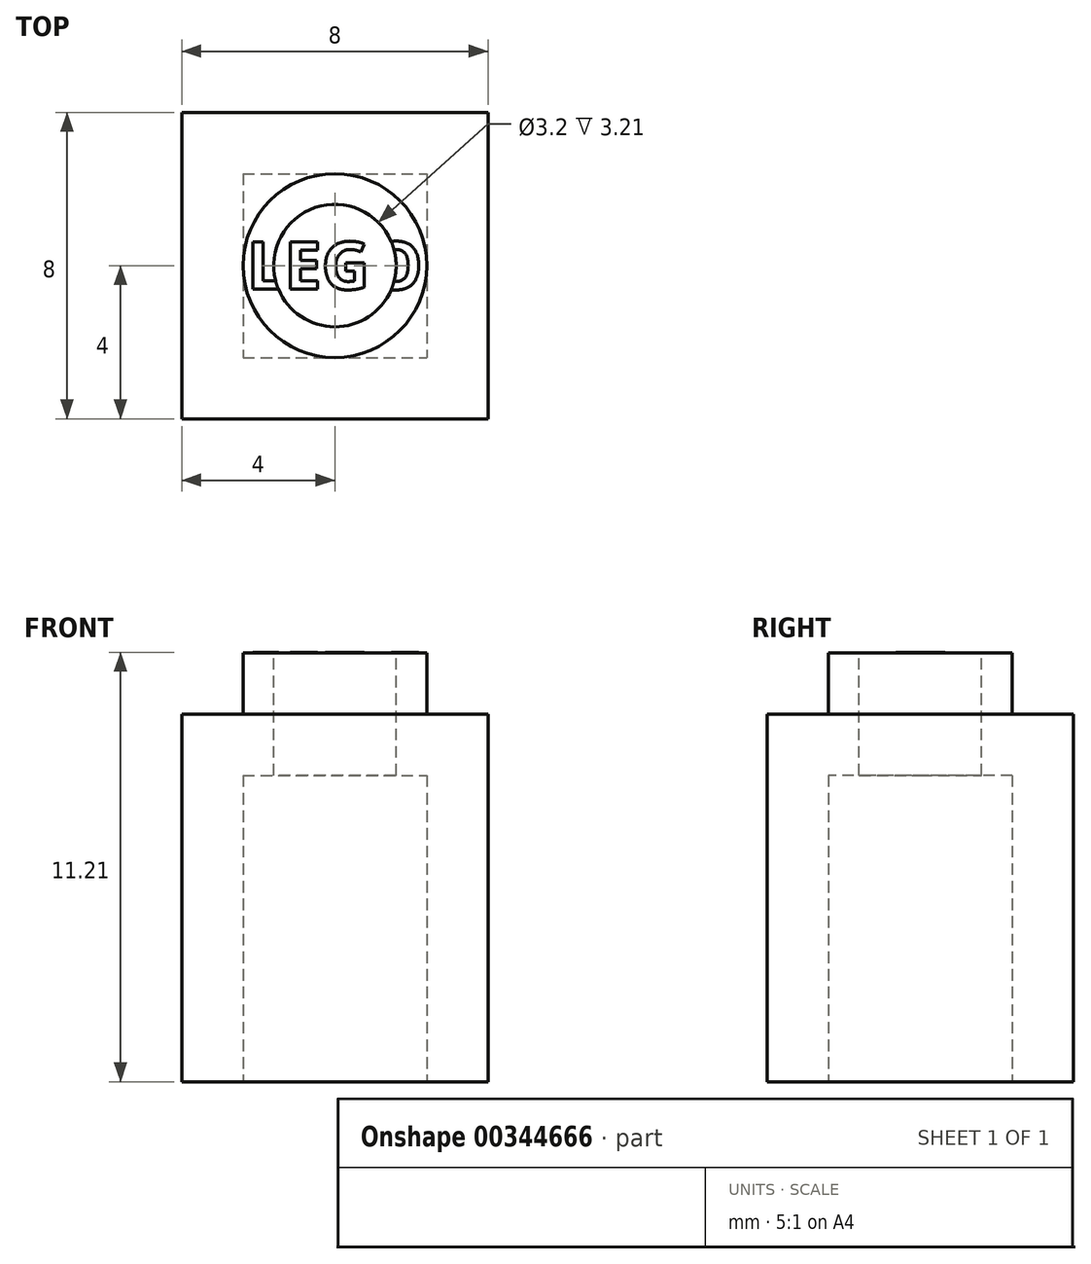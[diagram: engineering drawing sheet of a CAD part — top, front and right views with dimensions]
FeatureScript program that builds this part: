
annotation { "Feature Type Name" : "Feature", "Feature Type Description" : "" }
export const myFeature = defineFeature(function(context is Context, id is Id, definition is map)
    precondition{}
    {
        {
            var Q0;
            Q0=qCreatedBy(makeId("Top.planeOp"),FACE);
            var sketch = newSketch(context, id + "F0", { "sketchPlane" : qUnion([Q0])});
            skLineSegment(sketch, "E0.bottom", {"start": v(-4, 4) * mm, "end": v(4, 4) * mm});
            skLineSegment(sketch, "E0.top", {"start": v(-4, -4) * mm, "end": v(4, -4) * mm});
            skLineSegment(sketch, "E0.left", {"start": v(-4, 4) * mm, "end": v(-4, -4) * mm});
            skLineSegment(sketch, "E0.right", {"start": v(4, 4) * mm, "end": v(4, -4) * mm});
            skPoint(sketch, "E0.middle", {"position": v(0, 0) * mm});
            skSolve(sketch);
        }
        {
            var Q0;
            Q0=makeQuery(id+"F0.imprint","IMPRINT",FACE,{"disambiguationData":[TD([[makeQuery(id+"F0.imprint","IMPRINT",EDGE,{"derivedFrom":sQuery(id+"F0.wireOp",EDGE,"E0.bottom")}),-1.0]])]});
            extrude(context, id + "F1", {"entities" : qUnion([Q0]), "depth" : 9.6 * mm});
        }
        {
            var Q0;
            Q0=makeQuery(id+"F1.opExtrude","CAP_FACE",FACE,{"disambiguationData":[OSD([sQuery(id+"F0.wireOp",EDGE,"E0.bottom"),sQuery(id+"F0.wireOp",EDGE,"E0.top"),sQuery(id+"F0.wireOp",EDGE,"E0.left"),sQuery(id+"F0.wireOp",EDGE,"E0.right")])],"isStart":true});
            var sketch = newSketch(context, id + "F2", { "sketchPlane" : qUnion([Q0])});
            skLineSegment(sketch, "E1.bottom", {"start": v(-2.4, -2.4) * mm, "end": v(2.4, -2.4) * mm});
            skLineSegment(sketch, "E1.top", {"start": v(-2.4, 2.4) * mm, "end": v(2.4, 2.4) * mm});
            skLineSegment(sketch, "E1.left", {"start": v(-2.4, -2.4) * mm, "end": v(-2.4, 2.4) * mm});
            skLineSegment(sketch, "E1.right", {"start": v(2.4, -2.4) * mm, "end": v(2.4, 2.4) * mm});
            skPoint(sketch, "E1.middle", {"position": v(0, 0) * mm});
            skSolve(sketch);
        }
        {
            var Q0;
            Q0=makeQuery(id+"F2.imprint","IMPRINT",FACE,{"disambiguationData":[TD([[makeQuery(id+"F2.imprint","IMPRINT",EDGE,{"derivedFrom":sQuery(id+"F2.wireOp",EDGE,"E1.bottom")}),1.0]])]});
            extrude(context, id + "F3", {"entities" : qUnion([Q0]), "operationType" : NewBodyOperationType.REMOVE, "oppositeDirection" : true, "depth" : 8 * mm});
        }
        {
            var Q0;
            Q0=makeQuery(id+"F1.opExtrude","CAP_FACE",FACE,{"disambiguationData":[OSD([sQuery(id+"F0.wireOp",EDGE,"E0.bottom"),sQuery(id+"F0.wireOp",EDGE,"E0.top"),sQuery(id+"F0.wireOp",EDGE,"E0.left"),sQuery(id+"F0.wireOp",EDGE,"E0.right")])],"isStart":false});
            var sketch = newSketch(context, id + "F4", { "sketchPlane" : qUnion([Q0])});
            skCircle(sketch, "E2", {"center": v(0, 0) * mm, "radius": 1.6 * mm});
            skSolve(sketch);
        }
        {
            var Q0;
            Q0=makeQuery(id+"F4.imprint","IMPRINT",FACE,{"disambiguationData":[TD([[makeQuery(id+"F4.imprint","IMPRINT",EDGE,{"derivedFrom":sQuery(id+"F4.wireOp",EDGE,"E2")}),1.0]])]});
            extrude(context, id + "F5", {"entities" : qUnion([Q0]), "operationType" : NewBodyOperationType.REMOVE, "oppositeDirection" : true, "depth" : 1.6 * mm});
        }
        {
            var Q0;
            Q0=makeQuery(id+"F1.opExtrude","CAP_FACE",FACE,{"disambiguationData":[OSD([sQuery(id+"F0.wireOp",EDGE,"E0.bottom"),sQuery(id+"F0.wireOp",EDGE,"E0.top"),sQuery(id+"F0.wireOp",EDGE,"E0.left"),sQuery(id+"F0.wireOp",EDGE,"E0.right")])],"isStart":false});
            var sketch = newSketch(context, id + "F6", { "sketchPlane" : qUnion([Q0])});
            skCircle(sketch, "E3", {"center": v(0, 0) * mm, "radius": 2.4 * mm});
            skSolve(sketch);
        }
        {
            var Q0;
            Q0=makeQuery(id+"F6.imprint","IMPRINT",FACE,{"disambiguationData":[TD([[makeQuery(id+"F6.imprint","IMPRINT",EDGE,{"derivedFrom":makeQuery(id+"F5.boolean.opBoolean","COPY",EDGE,{"derivedFrom":makeQuery(id+"F5.opExtrude","CAP_EDGE",EDGE,{"disambiguationData":[OSD([sQuery(id+"F4.wireOp",EDGE,"E2")])],"isStart":true})})}),1.0]])]});
            var Q1;
            Q1=makeQuery(id+"F6.imprint","IMPRINT",FACE,{"disambiguationData":[TD([[makeQuery(id+"F6.imprint","IMPRINT",EDGE,{"derivedFrom":sQuery(id+"F6.wireOp",EDGE,"E3")}),1.0]])]});
            extrude(context, id + "F7", {"entities" : qUnion([Q0, Q1]), "operationType" : NewBodyOperationType.ADD, "depth" : 1.6 * mm});
        }
        {
            var Q0;
            Q0=makeQuery(id+"F7.opExtrude","CAP_FACE",FACE,{"disambiguationData":[OSD([sQuery(id+"F6.wireOp",EDGE,"E3")])],"isStart":false});
            var sketch = newSketch(context, id + "F8", { "sketchPlane" : qUnion([Q0])});
            skText(sketch, "E4", { "text": "LEGO", "fontName": "OpenSans-Bold.ttf"});
            const initialGuessF8  = {"E4": [-0.0023, -0.00062, 1, 0, 0.00125]};
            skSetInitialGuess(sketch, initialGuessF8);
            skSolve(sketch);
        }
        {
            var Q0;
            Q0=makeQuery(id+"F8.imprint","IMPRINT",FACE,{"disambiguationData":[TD([[makeQuery(id+"F8.imprint","IMPRINT",EDGE,{"derivedFrom":sQuery(id+"F8.wireOp",EDGE,"E4.sketch_text.stroke-0")}),-1.0]])]});
            var Q1;
            Q1=makeQuery(id+"F8.imprint","IMPRINT",FACE,{"disambiguationData":[TD([[makeQuery(id+"F8.imprint","IMPRINT",EDGE,{"derivedFrom":sQuery(id+"F8.wireOp",EDGE,"E4.sketch_text.stroke-6")}),-1.0]])]});
            var Q2;
            Q2=makeQuery(id+"F8.imprint","IMPRINT",FACE,{"disambiguationData":[TD([[makeQuery(id+"F8.imprint","IMPRINT",EDGE,{"derivedFrom":sQuery(id+"F8.wireOp",EDGE,"E4.sketch_text.stroke-18")}),-1.0]])]});
            var Q3;
            Q3=makeQuery(id+"F8.imprint","IMPRINT",FACE,{"disambiguationData":[TD([[makeQuery(id+"F8.imprint","IMPRINT",EDGE,{"derivedFrom":sQuery(id+"F8.wireOp",EDGE,"E4.sketch_text.stroke-37")}),-1.0]])]});
            extrude(context, id + "F9", {"entities" : qUnion([Q0, Q1, Q2, Q3]), "operationType" : NewBodyOperationType.ADD, "depth" : 0.01 * mm});
        }
    });
